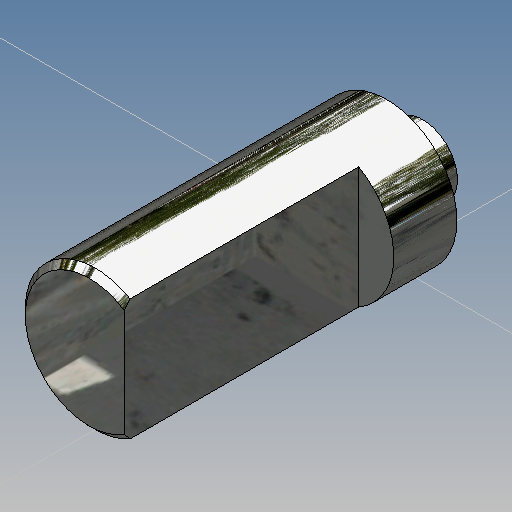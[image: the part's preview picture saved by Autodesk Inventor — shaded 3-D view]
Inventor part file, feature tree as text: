
AUTODESK INVENTOR PART (.ipt)
format: ipt  version: 2019 (Build 230136000, 136)  size: 207,360 bytes
history: native  units: in
note: dims shown in document units (in); Inventor stores cm internally (conversion verified against a paired STEP export)
features: extrude x3, sketch x3, chamfer x1
ambient origin geometry x8: Origin, YZ Plane, XZ Plane, XY Plane, X Axis, Y Axis, Z Axis, Center Point
bodies: Solid1 (feature_tree)
feature tree (7):
  extrude  "Extrusion1"  Depth=0.5in TaperAngle=0.0deg
  extrude  "Extrusion2"  Depth=0.0585in TaperAngle=0.0deg
  extrude  "Extrusion3"  Depth=0.06in TaperAngle=45.0deg
  chamfer  "Chamfer1"  [1 undecoded]
  sketch  "Sketch1"  dims[d0=0.235in d1=0.5in d2=0.0in]
  sketch  "Sketch2"  dims[d3=0.0585in d4=0.394in d5=0.0in]
  sketch  "Sketch3"  dims[d6=0.06in d7=0.0in d8=0.01in d9=0.125in d10=45.0deg]
note: 1 required parameter value undecoded (feature->parameter linkage not recoverable at this tier; creation-order binding heuristic only, values carry confidence <= 0.55)
